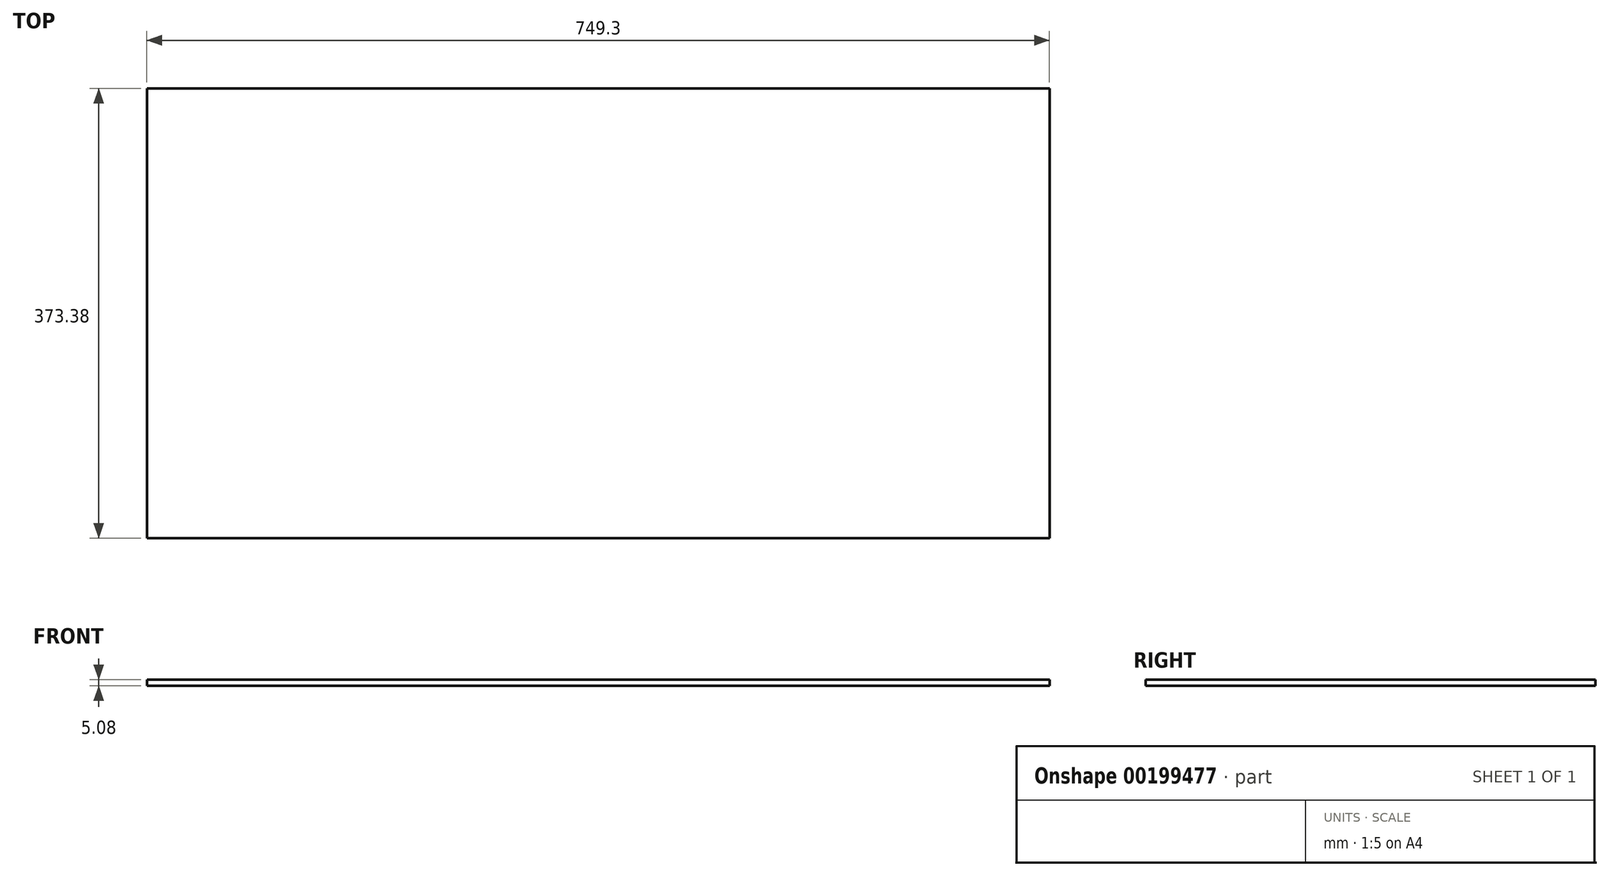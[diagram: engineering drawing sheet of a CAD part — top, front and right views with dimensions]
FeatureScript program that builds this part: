
annotation { "Feature Type Name" : "Feature", "Feature Type Description" : "" }
export const myFeature = defineFeature(function(context is Context, id is Id, definition is map)
    precondition{}
    {
        {
            var Q0;
            Q0=qCreatedBy(makeId("Top.planeOp"),FACE);
            var sketch = newSketch(context, id + "F0", { "sketchPlane" : qUnion([Q0])});
            skLineSegment(sketch, "E0.bottom", {"start": v(-337.99, 183.6) * mm, "end": v(411.31, 183.6) * mm});
            skLineSegment(sketch, "E0.top", {"start": v(-337.99, -189.77) * mm, "end": v(411.31, -189.77) * mm});
            skLineSegment(sketch, "E0.left", {"start": v(-337.99, 183.6) * mm, "end": v(-337.99, -189.77) * mm});
            skLineSegment(sketch, "E0.right", {"start": v(411.31, 183.6) * mm, "end": v(411.31, -189.77) * mm});
            skSolve(sketch);
        }
        {
            var Q0;
            Q0 = qSketchRegion(id + "F0", true);
            extrude(context, id + "F1", {"entities" : qUnion([Q0]), "depth" : 5.08 * mm});
        }
    });
